# Revit family: T100066
name_source: partatom
category: Furniture
revit_build: Autodesk Revit Architecture 2013 (Build: 20120221_2030(x64)
units: mm (PartAtom-declared; Revit-internal decimal feet)

## types (1)
- T100066
    Assembly Code = E2020200
    Back Coverage Material = OFS BRANDS STACKS Back Coverage Plastic
    Catalog = http://ofsbrands.com
    Chassis Material = OFS BRANDS STACKS Chassis Wood
    Conector Clip Material = OFS BRANDS STACKS Conector Clip Metal
    Cushion Material = OFS BRANDS STACKS Cushion Fabric
    Depth = 72"
    Description = OFS BRANDS FIRST OFFICE STACKS TYPICAL T100066
    Drawer Front Material = OFS BRANDS STACKS Drawer Front Wood
    Feet Material = OFS BRANDS STACKS Feet Metal
    Glides Material = OFS BRANDS STACKS Glide Plastic
    Grommet  Material = OFS BRANDS STACKS Grommet Metal
    Height = 72"
    Lock Material = OFS BRANDS STACKSLock Metal
    Manufacturer = FIRST OFFICE
    Model = T100066
    Pull Material = OFS BRANDS STACKS Pull Metal
    Roll Material = OFS BRANDS STACKS Roll Plastic
    Top Core Material = OFS BRANDS STACKS Top Core Wood
    URL = http://www.ofsbrands.com
    Width = 108"

## geometry (parser evidence)
native form markers: Blend x16, Sweep x1
no freeform markers — native parametric forms only
